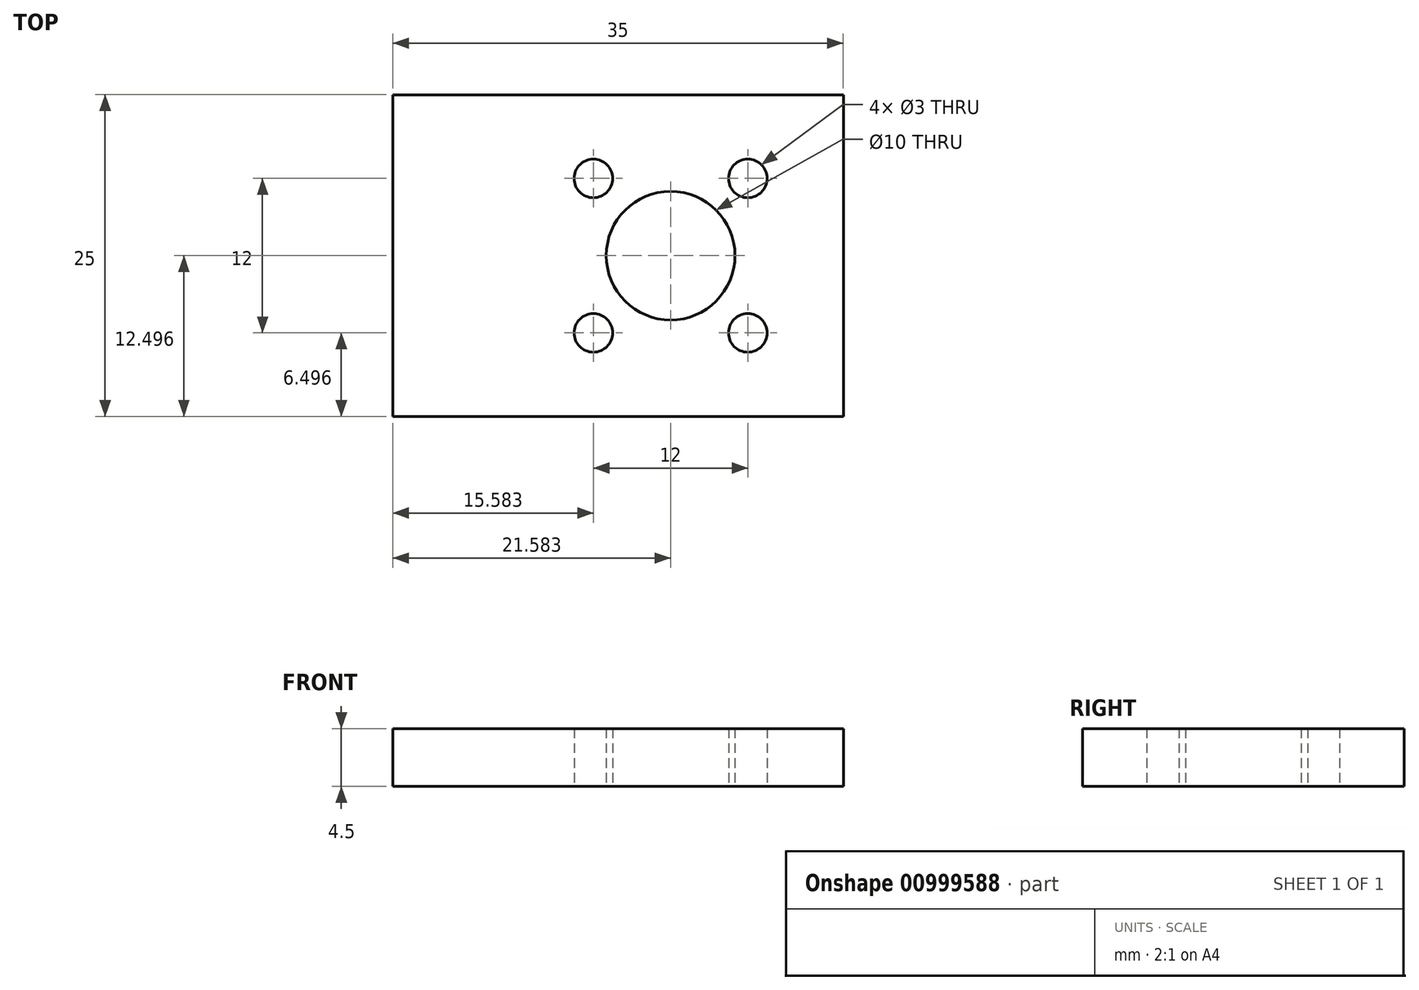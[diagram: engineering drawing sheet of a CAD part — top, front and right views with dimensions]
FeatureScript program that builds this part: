
annotation { "Feature Type Name" : "Feature", "Feature Type Description" : "" }
export const myFeature = defineFeature(function(context is Context, id is Id, definition is map)
    precondition{}
    {
        {
            var Q0;
            Q0=qCreatedBy(makeId("Top.planeOp"),FACE);
            var sketch = newSketch(context, id + "F0", { "sketchPlane" : qUnion([Q0])});
            skLineSegment(sketch, "E0", {"start": v(-62.6, 28.73) * mm, "end": v(-62.6, 3.73) * mm});
            skLineSegment(sketch, "E1", {"start": v(-62.6, 3.73) * mm, "end": v(-27.6, 3.73) * mm});
            skLineSegment(sketch, "E2", {"start": v(-27.6, 3.73) * mm, "end": v(-27.6, 28.73) * mm});
            skLineSegment(sketch, "E3", {"start": v(-27.6, 28.73) * mm, "end": v(-62.6, 28.73) * mm});
            skCircle(sketch, "E4", {"center": v(-41.02, 16.23) * mm, "radius": 5 * mm});
            skCircle(sketch, "E5", {"center": v(-35.02, 10.23) * mm, "radius": 1.5 * mm});
            skLineSegment(sketch, "E6", {"start": v(-64.9, 16.23) * mm, "end": v(-14.47, 16.23) * mm, "construction": true});
            skCircle(sketch, "E7", {"center": v(-35.02, 22.23) * mm, "radius": 1.5 * mm});
            skCircle(sketch, "E8", {"center": v(-47.02, 22.23) * mm, "radius": 1.5 * mm});
            skCircle(sketch, "E9", {"center": v(-47.02, 10.23) * mm, "radius": 1.5 * mm});
            skLineSegment(sketch, "E10", {"start": v(-41.02, 34.6) * mm, "end": v(-41.02, -2.88) * mm, "construction": true});
            skSolve(sketch);
        }
        {
            var Q0;
            Q0=makeQuery(id+"F0.imprint","IMPRINT",FACE,{"disambiguationData":[TD([[makeQuery(id+"F0.imprint","IMPRINT",EDGE,{"derivedFrom":sQuery(id+"F0.wireOp",EDGE,"E0")}),1.0]])]});
            extrude(context, id + "F1", {"entities" : qUnion([Q0]), "depth" : 4.5 * mm, "offsetDistance" : 25 * mm});
        }
    });
